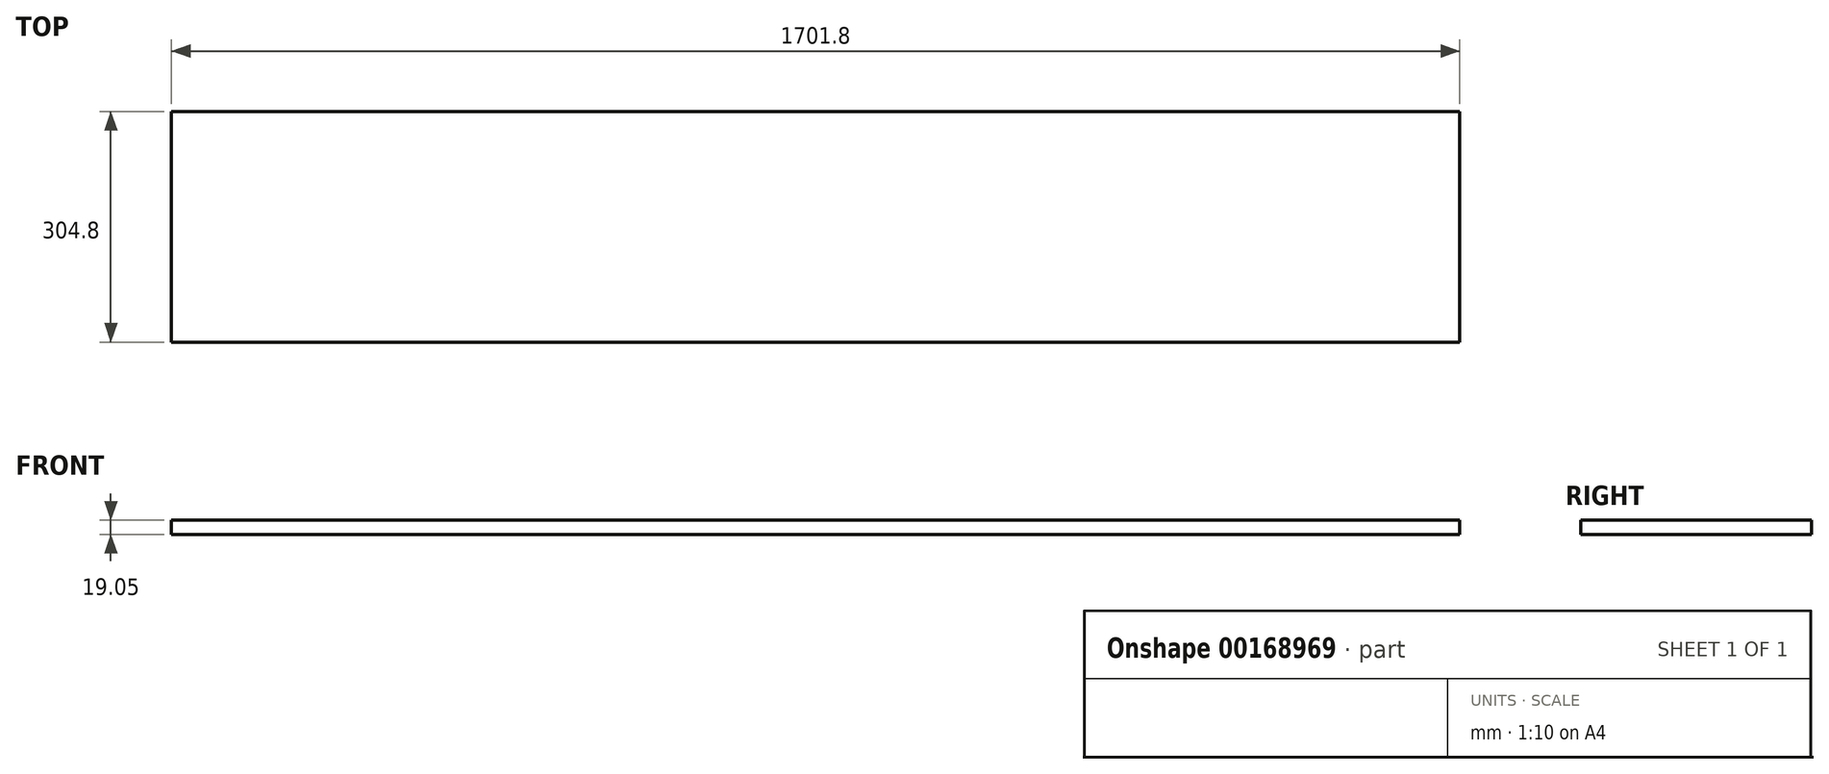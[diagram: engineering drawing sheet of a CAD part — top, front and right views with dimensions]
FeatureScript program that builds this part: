
annotation { "Feature Type Name" : "Feature", "Feature Type Description" : "" }
export const myFeature = defineFeature(function(context is Context, id is Id, definition is map)
    precondition{}
    {
        {
            var Q0;
            Q0=qCreatedBy(makeId("Top.planeOp"),FACE);
            var sketch = newSketch(context, id + "F0", { "sketchPlane" : qUnion([Q0])});
            skLineSegment(sketch, "E0.bottom", {"start": v(-786.42, 116.05) * mm, "end": v(915.38, 116.05) * mm});
            skLineSegment(sketch, "E0.top", {"start": v(-786.42, -188.75) * mm, "end": v(915.38, -188.75) * mm});
            skLineSegment(sketch, "E0.left", {"start": v(-786.42, 116.05) * mm, "end": v(-786.42, -188.75) * mm});
            skLineSegment(sketch, "E0.right", {"start": v(915.38, 116.05) * mm, "end": v(915.38, -188.75) * mm});
            skSolve(sketch);
        }
        {
            var Q0;
            Q0 = qSketchRegion(id + "F0", true);
            extrude(context, id + "F1", {"entities" : qUnion([Q0]), "depth" : 19.05 * mm});
        }
    });
